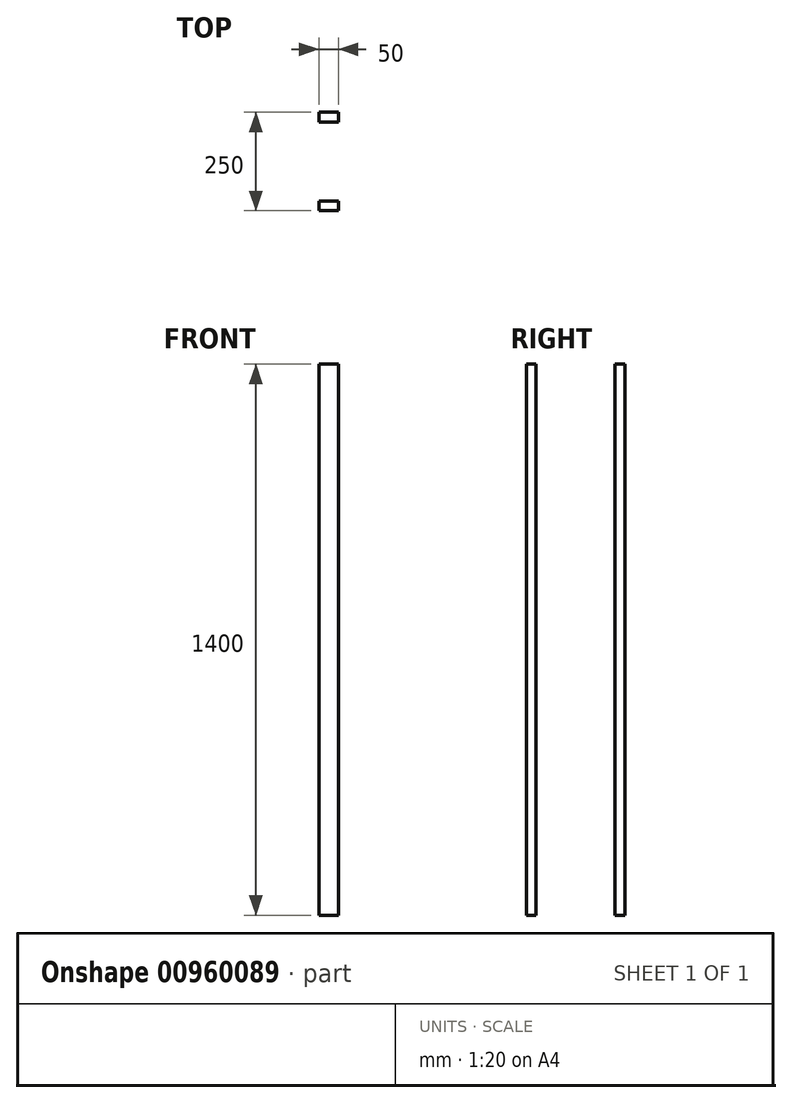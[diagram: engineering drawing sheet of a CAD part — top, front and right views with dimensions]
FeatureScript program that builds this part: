
annotation { "Feature Type Name" : "Feature", "Feature Type Description" : "" }
export const myFeature = defineFeature(function(context is Context, id is Id, definition is map)
    precondition{}
    {
        {
            var Q0;
            Q0=qCreatedBy(makeId("Top.planeOp"),FACE);
            var sketch = newSketch(context, id + "F0", { "sketchPlane" : qUnion([Q0])});
            skLineSegment(sketch, "E0.bottom", {"start": v(-31.1, 17.2) * mm, "end": v(18.9, 17.2) * mm});
            skLineSegment(sketch, "E0.top", {"start": v(-31.1, -7.8) * mm, "end": v(18.9, -7.8) * mm});
            skLineSegment(sketch, "E0.left", {"start": v(-31.1, 17.2) * mm, "end": v(-31.1, -7.8) * mm});
            skLineSegment(sketch, "E0.right", {"start": v(18.9, 17.2) * mm, "end": v(18.9, -7.8) * mm});
            skLineSegment(sketch, "E1.bottom", {"start": v(-31.1, -207.8) * mm, "end": v(18.9, -207.8) * mm});
            skLineSegment(sketch, "E1.top", {"start": v(-31.1, -232.8) * mm, "end": v(18.9, -232.8) * mm});
            skLineSegment(sketch, "E1.left", {"start": v(-31.1, -207.8) * mm, "end": v(-31.1, -232.8) * mm});
            skLineSegment(sketch, "E1.right", {"start": v(18.9, -207.8) * mm, "end": v(18.9, -232.8) * mm});
            skLineSegment(sketch, "E2.left", {"start": v(-31.1, -7.8) * mm, "end": v(-31.1, -207.8) * mm});
            skLineSegment(sketch, "E2.right", {"start": v(18.9, -7.8) * mm, "end": v(18.9, -207.8) * mm});
            skSolve(sketch);
        }
        {
            var Q0;
            Q0=makeQuery(id+"F0.imprint","IMPRINT",FACE,{"disambiguationData":[TD([[makeQuery(id+"F0.imprint","IMPRINT",EDGE,{"derivedFrom":sQuery(id+"F0.wireOp",EDGE,"E0.bottom")}),-1.0]])]});
            var Q1;
            Q1=makeQuery(id+"F0.imprint","IMPRINT",FACE,{"disambiguationData":[TD([[makeQuery(id+"F0.imprint","IMPRINT",EDGE,{"derivedFrom":sQuery(id+"F0.wireOp",EDGE,"E1.top")}),1.0]])]});
            extrude(context, id + "F1", {"entities" : qUnion([Q0, Q1]), "oppositeDirection" : true, "depth" : 1400 * mm, "offsetDistance" : 25 * mm});
        }
    });
